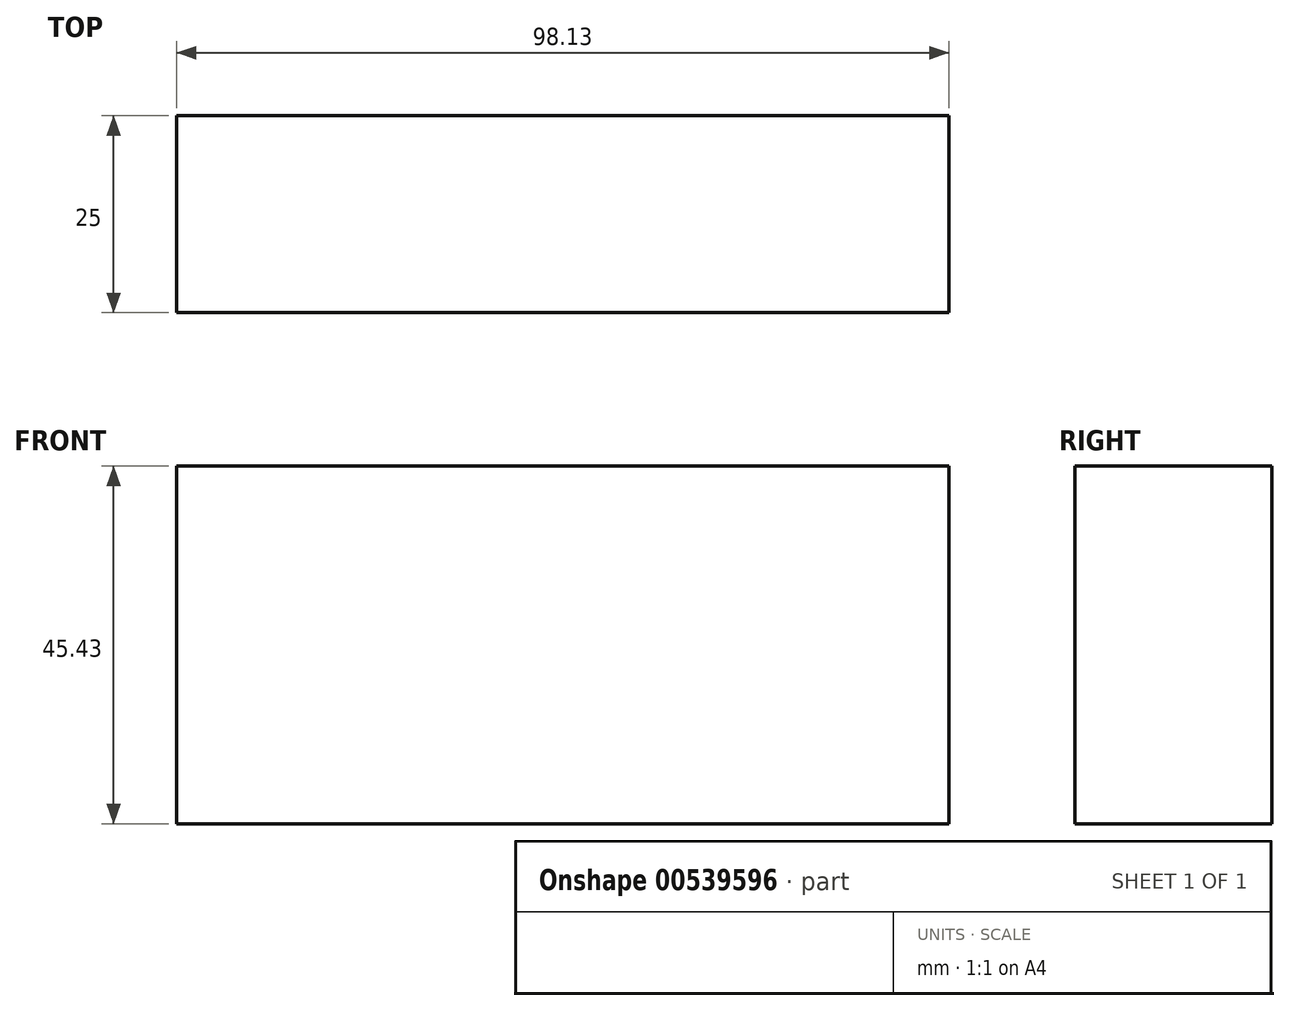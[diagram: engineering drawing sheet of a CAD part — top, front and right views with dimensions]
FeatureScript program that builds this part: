
annotation { "Feature Type Name" : "Feature", "Feature Type Description" : "" }
export const myFeature = defineFeature(function(context is Context, id is Id, definition is map)
    precondition{}
    {
        {
            var Q0;
            Q0=qCreatedBy(makeId("Front.planeOp"),FACE);
            var sketch = newSketch(context, id + "F0", { "sketchPlane" : qUnion([Q0])});
            skLineSegment(sketch, "E0.bottom", {"start": v(-136.52, 22.67) * mm, "end": v(-38.39, 22.67) * mm});
            skLineSegment(sketch, "E0.top", {"start": v(-136.52, -22.76) * mm, "end": v(-38.39, -22.76) * mm});
            skLineSegment(sketch, "E0.left", {"start": v(-136.52, 22.67) * mm, "end": v(-136.52, -22.76) * mm});
            skLineSegment(sketch, "E0.right", {"start": v(-38.39, 22.67) * mm, "end": v(-38.39, -22.76) * mm});
            skSolve(sketch);
        }
        {
            var Q0;
            Q0 = qSketchRegion(id + "F0", true);
            extrude(context, id + "F1", {"entities" : qUnion([Q0]), "depth" : 25 * mm, "offsetDistance" : 25 * mm});
        }
    });
